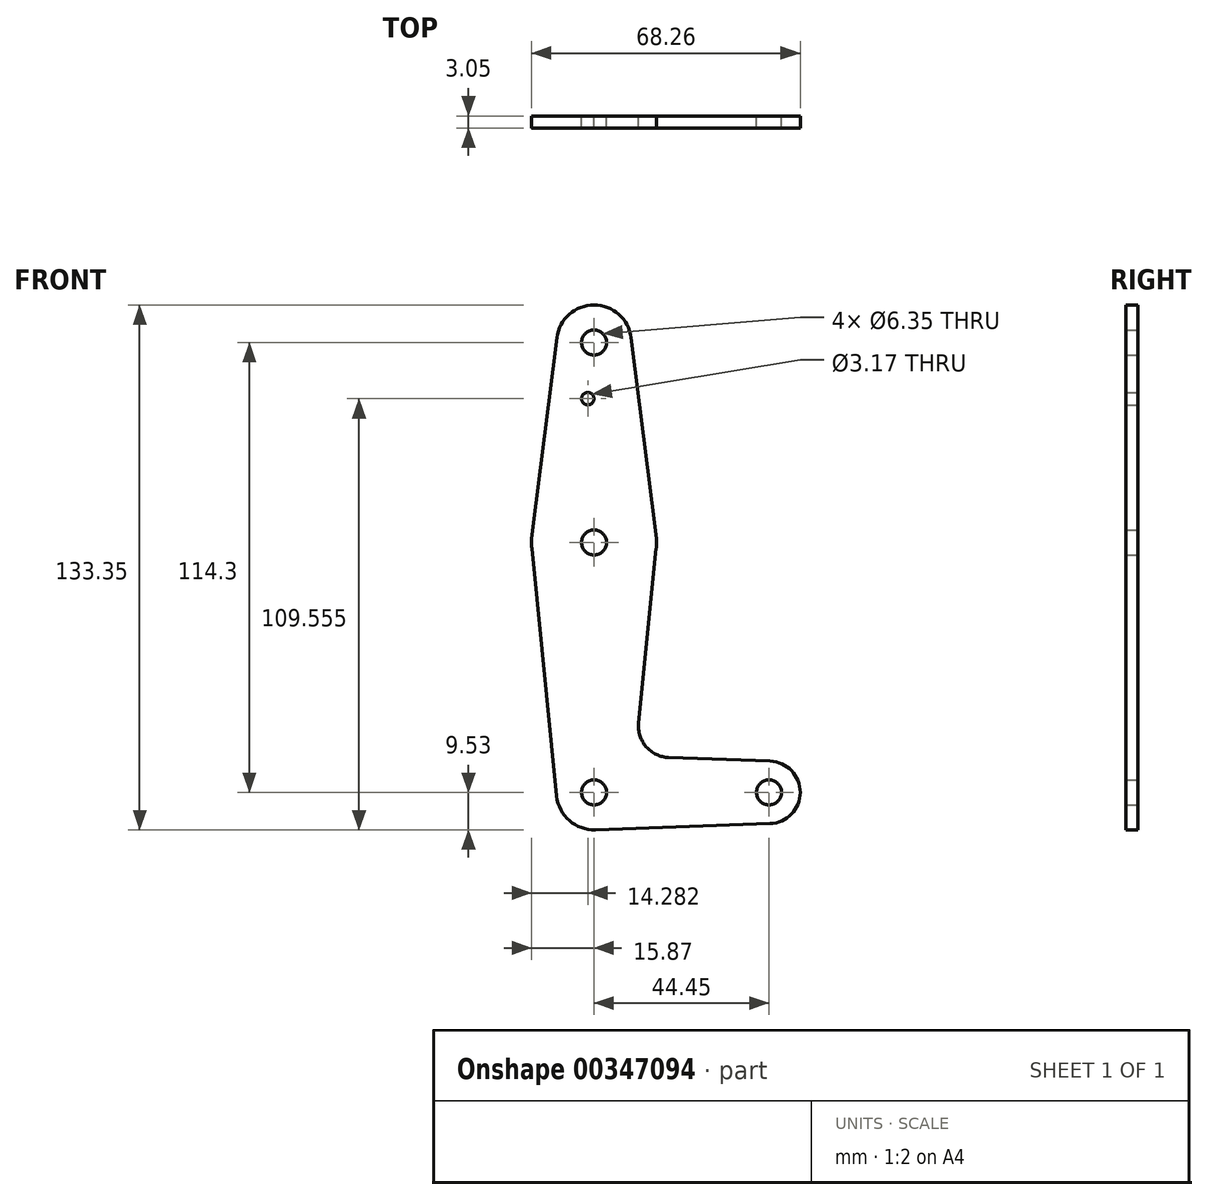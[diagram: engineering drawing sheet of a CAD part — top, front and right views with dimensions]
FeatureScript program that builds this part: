
annotation { "Feature Type Name" : "Feature", "Feature Type Description" : "" }
export const myFeature = defineFeature(function(context is Context, id is Id, definition is map)
    precondition{}
    {
        {
            var Q0;
            Q0=qCreatedBy(makeId("Front.planeOp"),FACE);
            var sketch = newSketch(context, id + "F0", { "sketchPlane" : qUnion([Q0])});
            skCircle(sketch, "E0", {"center": v(0, 0) * mm, "radius": 15.88 * mm});
            skCircle(sketch, "E1", {"center": v(0, 50.8) * mm, "radius": 9.53 * mm});
            skCircle(sketch, "E2", {"center": v(0, -63.5) * mm, "radius": 9.53 * mm});
            skCircle(sketch, "E3", {"center": v(44.45, -63.5) * mm, "radius": 7.94 * mm});
            skLineSegment(sketch, "E4", {"start": v(0, 50.8) * mm, "end": v(0, -63.5) * mm, "construction": true});
            skLineSegment(sketch, "E5", {"start": v(0, -63.5) * mm, "end": v(44.45, -63.5) * mm, "construction": true});
            skLineSegment(sketch, "E6", {"start": v(0, 0) * mm, "end": v(0, -63.5) * mm, "construction": true});
            skLineSegment(sketch, "E7", {"start": v(44.73, -55.57) * mm, "end": v(18.97, -54.65) * mm});
            skLineSegment(sketch, "E8", {"start": v(0.34, -73.02) * mm, "end": v(44.73, -71.43) * mm});
            skLineSegment(sketch, "E9", {"start": v(-9.48, -64.45) * mm, "end": v(-15.8, -1.59) * mm});
            skLineSegment(sketch, "E10", {"start": v(15.8, -1.59) * mm, "end": v(11.34, -45.9) * mm});
            skLineSegment(sketch, "E11", {"start": v(-9.45, 52) * mm, "end": v(-15.75, 1.98) * mm});
            skLineSegment(sketch, "E12", {"start": v(9.45, 52) * mm, "end": v(15.75, 1.98) * mm});
            skCircle(sketch, "E13", {"center": v(0, 50.8) * mm, "radius": 3.18 * mm});
            skCircle(sketch, "E14", {"center": v(0, 0) * mm, "radius": 3.18 * mm});
            skCircle(sketch, "E15", {"center": v(0, -63.5) * mm, "radius": 3.18 * mm});
            skCircle(sketch, "E16", {"center": v(44.45, -63.5) * mm, "radius": 3.18 * mm});
            skCircle(sketch, "E17", {"center": v(-1.59, 36.53) * mm, "radius": 1.59 * mm});
            skLineSegment(sketch, "E18", {"start": v(0, 0) * mm, "end": v(0, 36.53) * mm, "construction": true});
            skArc(sketch, "E19.filletArc", {"start": v(11.34, -45.9) * mm, "mid": v(13.26, -51.93) * mm, "end": v(18.97, -54.65) * mm});
            skSolve(sketch);
        }
        {
            var Q0;
            Q0 = qSketchRegion(id + "F0", true);
            extrude(context, id + "F1", {"entities" : qUnion([Q0]), "depth" : 3.05 * mm});
        }
    });
